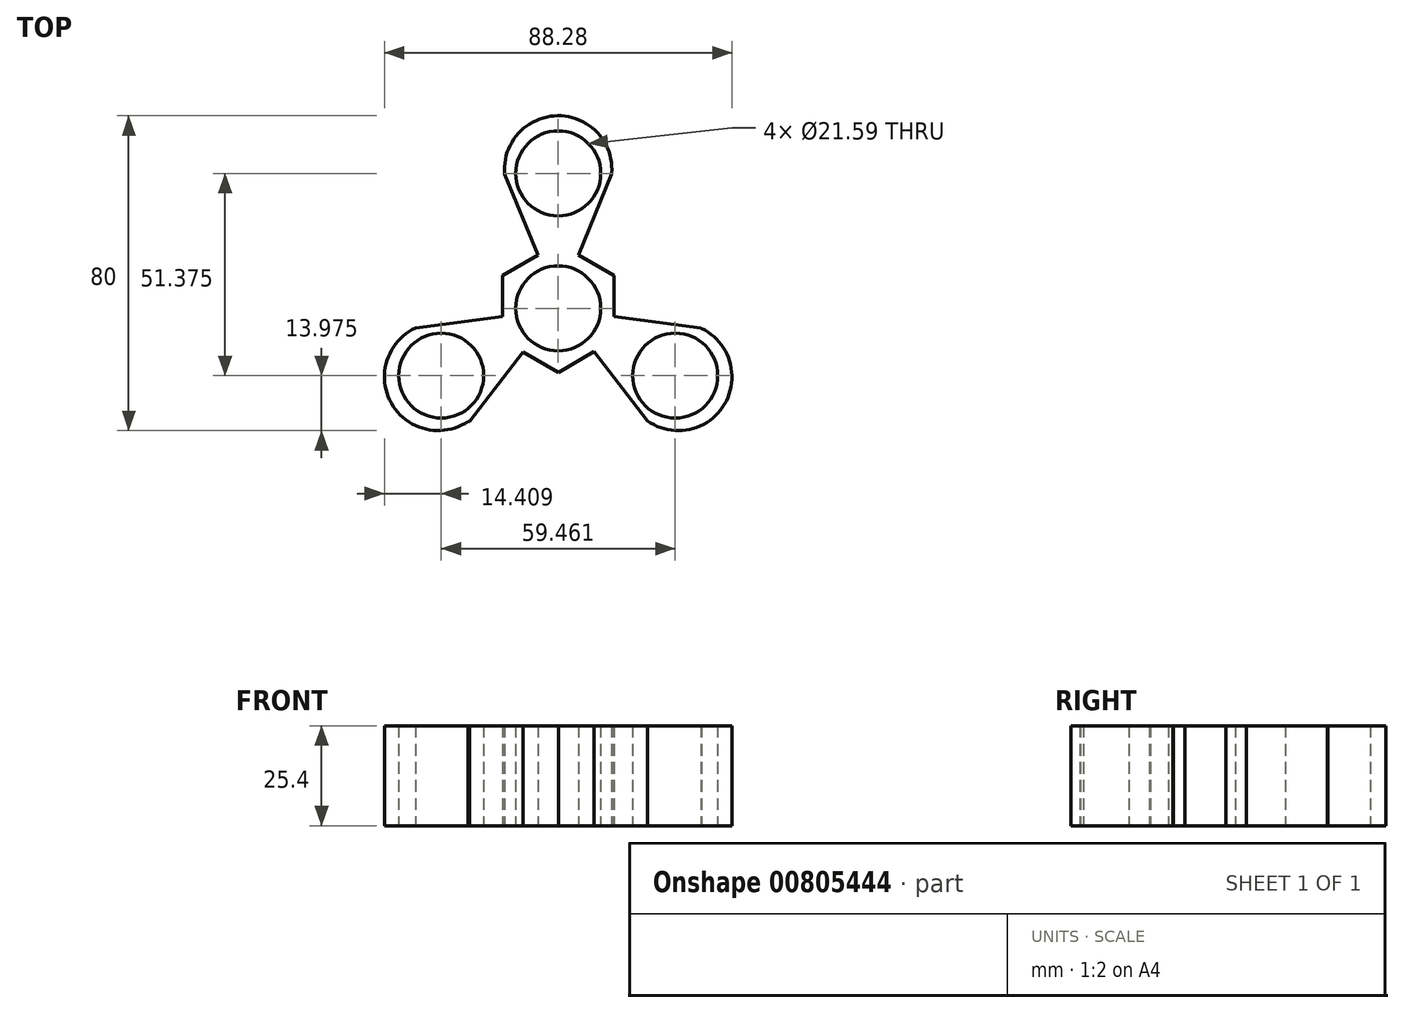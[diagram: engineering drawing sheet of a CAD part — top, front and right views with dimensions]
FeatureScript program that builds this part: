
annotation { "Feature Type Name" : "Feature", "Feature Type Description" : "" }
export const myFeature = defineFeature(function(context is Context, id is Id, definition is map)
    precondition{}
    {
        {
            var Q0;
            Q0=qCreatedBy(makeId("Top.planeOp"),FACE);
            var sketch = newSketch(context, id + "F0", { "sketchPlane" : qUnion([Q0])});
            skCircle(sketch, "E0", {"center": v(0, 0) * mm, "radius": 10.8 * mm});
            skLineSegment(sketch, "E1", {"start": v(0, 34.3) * mm, "end": v(-8, 20.47) * mm});
            skLineSegment(sketch, "E2", {"start": v(-29.73, -17.08) * mm, "end": v(-13.6, -17.08) * mm});
            skLineSegment(sketch, "E3", {"start": v(29.73, -17.08) * mm, "end": v(21.63, -3.09) * mm});
            skCircle(sketch, "E4", {"center": v(0, 34.3) * mm, "radius": 10.8 * mm});
            skCircle(sketch, "E5", {"center": v(-29.73, -17.08) * mm, "radius": 10.8 * mm});
            skCircle(sketch, "E6", {"center": v(29.73, -17.08) * mm, "radius": 10.8 * mm});
            skArc(sketch, "E7", {"start": v(13.6, 34.3) * mm, "mid": v(-0.12, 48.94) * mm, "end": v(-13.6, 34.07) * mm});
            skLineSegment(sketch, "E8", {"start": v(0, 61.27) * mm, "end": v(0, -54.26) * mm});
            skPoint(sketch, "E8.endSnap0", {"position": v(0, -17.08) * mm});
            skLineSegment(sketch, "E9", {"start": v(29.73, -17.08) * mm, "end": v(-43.23, 25.13) * mm});
            skLineSegment(sketch, "E10", {"start": v(-29.73, -17.08) * mm, "end": v(41.97, 24.4) * mm});
            skArc(sketch, "E11.MirrorCS", {"start": v(36.4, -5.11) * mm, "mid": v(42.27, -24.3) * mm, "end": v(22.66, -28.59) * mm});
            skArc(sketch, "E12.MirrorCS", {"start": v(-22.85, -28.7) * mm, "mid": v(-42.39, -24.1) * mm, "end": v(-36.21, -5) * mm});
            skLineSegment(sketch, "E13", {"start": v(-36.21, -5) * mm, "end": v(-14.16, -2.1) * mm});
            skLineSegment(sketch, "E14.MirrorCS", {"start": v(-13.6, 34.07) * mm, "end": v(-5.13, 13.5) * mm});
            skLineSegment(sketch, "E15.MirrorCS", {"start": v(13.6, 34.07) * mm, "end": v(5.13, 13.5) * mm});
            skLineSegment(sketch, "E16.MirrorCS", {"start": v(-0.1, 34.47) * mm, "end": v(8, 20.47) * mm});
            skLineSegment(sketch, "E17.MirrorCS", {"start": v(36.21, -5) * mm, "end": v(14.16, -2.1) * mm});
            skLineSegment(sketch, "E18.MirrorCS", {"start": v(22.66, -28.59) * mm, "end": v(9.05, -11) * mm});
            skLineSegment(sketch, "E19.MirrorCS", {"start": v(-22.48, -28.72) * mm, "end": v(-8.98, -11.05) * mm});
            skLineSegment(sketch, "E20", {"start": v(-14.16, -2.1) * mm, "end": v(-14.16, 8.31) * mm});
            skLineSegment(sketch, "E21", {"start": v(-14.16, 8.31) * mm, "end": v(-5.13, 13.5) * mm});
            skLineSegment(sketch, "E22.MirrorCS", {"start": v(14.16, 8.31) * mm, "end": v(5.13, 13.5) * mm});
            skLineSegment(sketch, "E23.MirrorCS", {"start": v(14.16, -2.1) * mm, "end": v(14.16, 8.31) * mm});
            skLineSegment(sketch, "E24.MirrorCS", {"start": v(-8.98, -11.05) * mm, "end": v(0.05, -16.24) * mm});
            skLineSegment(sketch, "E25.MirrorCS", {"start": v(0.05, -16.24) * mm, "end": v(9.05, -11) * mm});
            skLineSegment(sketch, "E26", {"start": v(13.6, 34.3) * mm, "end": v(13.6, 34.07) * mm});
            skLineSegment(sketch, "E27", {"start": v(-22.85, -28.7) * mm, "end": v(-22.48, -28.72) * mm});
            skLineSegment(sketch, "E28", {"start": v(36.21, -5) * mm, "end": v(36.4, -5.11) * mm});
            skLineSegment(sketch, "E29.trimOffspring", {"start": v(-21.63, -3.09) * mm, "end": v(-29.73, -17.08) * mm});
            skLineSegment(sketch, "E30.trimOffspring", {"start": v(21.63, -3.09) * mm, "end": v(29.63, -16.9) * mm});
            skLineSegment(sketch, "E31.trimOffspring", {"start": v(13.76, -17.08) * mm, "end": v(29.73, -17.08) * mm});
            skLineSegment(sketch, "E32.trimOffspring", {"start": v(8, 20.47) * mm, "end": v(0, 34.3) * mm});
            skSolve(sketch);
        }
        {
            var Q0;
            {var subQ0=sQuery(id+"F0.wireOp",EDGE,"E12.MirrorCS");Q0=makeQuery(id+"F0.imprint","IMPRINT",FACE,{"disambiguationData":[TD([[makeQuery(id+"F0.imprint","IMPRINT",EDGE,{"derivedFrom":subQ0}),-1.0]])]});}
            var Q1;
            {var subQ5=sQuery(id+"F0.wireOp",EDGE,"E2");var subQ11=sQuery(id+"F0.wireOp",EDGE,"E19.MirrorCS");var subQ12=makeQuery(id+"F0.imprint","INTERSECT",VERTEX,{"derivedFrom":[subQ5,subQ11]});Q1=makeQuery(id+"F0.imprint","IMPRINT",FACE,{"disambiguationData":[TD([[makeQuery(id+"F0.imprint","IMPRINT",EDGE,{"disambiguationData":[TD([[subQ12,1.0]])],"derivedFrom":subQ5}),1.0]])]});}
            var Q2;
            {var subQ0=sQuery(id+"F0.wireOp",EDGE,"E20");Q2=makeQuery(id+"F0.imprint","IMPRINT",FACE,{"disambiguationData":[TD([[makeQuery(id+"F0.imprint","IMPRINT",EDGE,{"derivedFrom":subQ0}),-1.0]])]});}
            var Q3;
            {var subQ0=sQuery(id+"F0.wireOp",EDGE,"E21");Q3=makeQuery(id+"F0.imprint","IMPRINT",FACE,{"disambiguationData":[TD([[makeQuery(id+"F0.imprint","IMPRINT",EDGE,{"derivedFrom":subQ0}),-1.0]])]});}
            var Q4;
            {var subQ0=sQuery(id+"F0.wireOp",EDGE,"E22.MirrorCS");Q4=makeQuery(id+"F0.imprint","IMPRINT",FACE,{"disambiguationData":[TD([[makeQuery(id+"F0.imprint","IMPRINT",EDGE,{"derivedFrom":subQ0}),1.0]])]});}
            var Q5;
            {var subQ5=sQuery(id+"F0.wireOp",EDGE,"E26");Q5=makeQuery(id+"F0.imprint","IMPRINT",FACE,{"disambiguationData":[TD([[makeQuery(id+"F0.imprint","IMPRINT",EDGE,{"derivedFrom":subQ5}),-1.0]])]});}
            var Q6;
            {var subQ5=sQuery(id+"F0.wireOp",EDGE,"E1");var subQ7=sQuery(id+"F0.wireOp",EDGE,"E14.MirrorCS");var subQ9=makeQuery(id+"F0.imprint","INTERSECT",VERTEX,{"derivedFrom":[subQ5,subQ7]});Q6=makeQuery(id+"F0.imprint","IMPRINT",FACE,{"disambiguationData":[TD([[makeQuery(id+"F0.imprint","IMPRINT",EDGE,{"disambiguationData":[TD([[subQ9,1.0]])],"derivedFrom":subQ5}),-1.0]])]});}
            var Q7;
            {var subQ0=sQuery(id+"F0.wireOp",EDGE,"E23.MirrorCS");Q7=makeQuery(id+"F0.imprint","IMPRINT",FACE,{"disambiguationData":[TD([[makeQuery(id+"F0.imprint","IMPRINT",EDGE,{"derivedFrom":subQ0}),1.0]])]});}
            var Q8;
            {var subQ0=sQuery(id+"F0.wireOp",EDGE,"E25.MirrorCS");Q8=makeQuery(id+"F0.imprint","IMPRINT",FACE,{"disambiguationData":[TD([[makeQuery(id+"F0.imprint","IMPRINT",EDGE,{"derivedFrom":subQ0}),1.0]])]});}
            var Q9;
            {var subQ5=sQuery(id+"F0.wireOp",EDGE,"E11.MirrorCS");Q9=makeQuery(id+"F0.imprint","IMPRINT",FACE,{"disambiguationData":[TD([[makeQuery(id+"F0.imprint","IMPRINT",EDGE,{"derivedFrom":subQ5}),-1.0]])]});}
            extrude(context, id + "F1", {"entities" : qUnion([Q0, Q1, Q2, Q3, Q4, Q5, Q6, Q7, Q8, Q9]), "depth" : 6.92 * mm, "offsetDistance" : 25.4 * mm});
        }
        {
            var Q0;
            Q0=makeQuery(id+"F1.opExtrude","CAP_FACE",FACE,{"disambiguationData":[OSD([sQuery(id+"F0.wireOp",EDGE,"E4"),sQuery(id+"F0.wireOp",EDGE,"E5"),sQuery(id+"F0.wireOp",EDGE,"E6"),sQuery(id+"F0.wireOp",EDGE,"E7"),sQuery(id+"F0.wireOp",EDGE,"E11.MirrorCS"),sQuery(id+"F0.wireOp",EDGE,"E12.MirrorCS"),sQuery(id+"F0.wireOp",EDGE,"E13"),sQuery(id+"F0.wireOp",EDGE,"E14.MirrorCS"),sQuery(id+"F0.wireOp",EDGE,"E15.MirrorCS"),sQuery(id+"F0.wireOp",EDGE,"E17.MirrorCS"),sQuery(id+"F0.wireOp",EDGE,"E18.MirrorCS"),sQuery(id+"F0.wireOp",EDGE,"E19.MirrorCS"),sQuery(id+"F0.wireOp",EDGE,"E20"),sQuery(id+"F0.wireOp",EDGE,"E21"),sQuery(id+"F0.wireOp",EDGE,"E0"),sQuery(id+"F0.wireOp",EDGE,"E22.MirrorCS"),sQuery(id+"F0.wireOp",EDGE,"E23.MirrorCS"),sQuery(id+"F0.wireOp",EDGE,"E24.MirrorCS"),sQuery(id+"F0.wireOp",EDGE,"E25.MirrorCS"),sQuery(id+"F0.wireOp",EDGE,"E26"),sQuery(id+"F0.wireOp",EDGE,"E27"),sQuery(id+"F0.wireOp",EDGE,"E28")])],"isStart":false});
            var Q1;
            Q1=makeQuery(id+"F1.opExtrude","CAP_FACE",FACE,{"disambiguationData":[OSD([sQuery(id+"F0.wireOp",EDGE,"E4"),sQuery(id+"F0.wireOp",EDGE,"E5"),sQuery(id+"F0.wireOp",EDGE,"E6"),sQuery(id+"F0.wireOp",EDGE,"E7"),sQuery(id+"F0.wireOp",EDGE,"E11.MirrorCS"),sQuery(id+"F0.wireOp",EDGE,"E12.MirrorCS"),sQuery(id+"F0.wireOp",EDGE,"E13"),sQuery(id+"F0.wireOp",EDGE,"E14.MirrorCS"),sQuery(id+"F0.wireOp",EDGE,"E15.MirrorCS"),sQuery(id+"F0.wireOp",EDGE,"E17.MirrorCS"),sQuery(id+"F0.wireOp",EDGE,"E18.MirrorCS"),sQuery(id+"F0.wireOp",EDGE,"E19.MirrorCS"),sQuery(id+"F0.wireOp",EDGE,"E20"),sQuery(id+"F0.wireOp",EDGE,"E21"),sQuery(id+"F0.wireOp",EDGE,"E0"),sQuery(id+"F0.wireOp",EDGE,"E22.MirrorCS"),sQuery(id+"F0.wireOp",EDGE,"E23.MirrorCS"),sQuery(id+"F0.wireOp",EDGE,"E24.MirrorCS"),sQuery(id+"F0.wireOp",EDGE,"E25.MirrorCS"),sQuery(id+"F0.wireOp",EDGE,"E26"),sQuery(id+"F0.wireOp",EDGE,"E27"),sQuery(id+"F0.wireOp",EDGE,"E28")])],"isStart":true});
            fillet(context, id + "F2", {"entities" : qUnion([Q0, Q1]), "radius" : 1.27 * mm, "tangentPropagation" : true, "allowEdgeOverflow" : false});
        }
        {
            var Q0;
            Q0 = qSketchRegion(id + "F0", true);
            var Q1;
            Q1=makeQuery(id+"F2.opFillet","SPLIT",FACE,{"disambiguationData":[OD(0.0)],"derivedFrom":makeQuery(id+"F1.opExtrude","CAP_FACE",FACE,{"disambiguationData":[OSD([sQuery(id+"F0.wireOp",EDGE,"E4"),sQuery(id+"F0.wireOp",EDGE,"E5"),sQuery(id+"F0.wireOp",EDGE,"E6"),sQuery(id+"F0.wireOp",EDGE,"E7"),sQuery(id+"F0.wireOp",EDGE,"E11.MirrorCS"),sQuery(id+"F0.wireOp",EDGE,"E12.MirrorCS"),sQuery(id+"F0.wireOp",EDGE,"E13"),sQuery(id+"F0.wireOp",EDGE,"E14.MirrorCS"),sQuery(id+"F0.wireOp",EDGE,"E15.MirrorCS"),sQuery(id+"F0.wireOp",EDGE,"E17.MirrorCS"),sQuery(id+"F0.wireOp",EDGE,"E18.MirrorCS"),sQuery(id+"F0.wireOp",EDGE,"E19.MirrorCS"),sQuery(id+"F0.wireOp",EDGE,"E20"),sQuery(id+"F0.wireOp",EDGE,"E21"),sQuery(id+"F0.wireOp",EDGE,"E0"),sQuery(id+"F0.wireOp",EDGE,"E22.MirrorCS"),sQuery(id+"F0.wireOp",EDGE,"E23.MirrorCS"),sQuery(id+"F0.wireOp",EDGE,"E24.MirrorCS"),sQuery(id+"F0.wireOp",EDGE,"E25.MirrorCS"),sQuery(id+"F0.wireOp",EDGE,"E26"),sQuery(id+"F0.wireOp",EDGE,"E27"),sQuery(id+"F0.wireOp",EDGE,"E28")])],"isStart":false})});
            var Q2;
            Q2=makeQuery(id+"F2.opFillet","SPLIT",FACE,{"disambiguationData":[OD(2.0)],"derivedFrom":makeQuery(id+"F1.opExtrude","CAP_FACE",FACE,{"disambiguationData":[OSD([sQuery(id+"F0.wireOp",EDGE,"E4"),sQuery(id+"F0.wireOp",EDGE,"E5"),sQuery(id+"F0.wireOp",EDGE,"E6"),sQuery(id+"F0.wireOp",EDGE,"E7"),sQuery(id+"F0.wireOp",EDGE,"E11.MirrorCS"),sQuery(id+"F0.wireOp",EDGE,"E12.MirrorCS"),sQuery(id+"F0.wireOp",EDGE,"E13"),sQuery(id+"F0.wireOp",EDGE,"E14.MirrorCS"),sQuery(id+"F0.wireOp",EDGE,"E15.MirrorCS"),sQuery(id+"F0.wireOp",EDGE,"E17.MirrorCS"),sQuery(id+"F0.wireOp",EDGE,"E18.MirrorCS"),sQuery(id+"F0.wireOp",EDGE,"E19.MirrorCS"),sQuery(id+"F0.wireOp",EDGE,"E20"),sQuery(id+"F0.wireOp",EDGE,"E21"),sQuery(id+"F0.wireOp",EDGE,"E0"),sQuery(id+"F0.wireOp",EDGE,"E22.MirrorCS"),sQuery(id+"F0.wireOp",EDGE,"E23.MirrorCS"),sQuery(id+"F0.wireOp",EDGE,"E24.MirrorCS"),sQuery(id+"F0.wireOp",EDGE,"E25.MirrorCS"),sQuery(id+"F0.wireOp",EDGE,"E26"),sQuery(id+"F0.wireOp",EDGE,"E27"),sQuery(id+"F0.wireOp",EDGE,"E28")])],"isStart":false})});
            extrude(context, id + "F3", {"entities" : qUnion([Q0, Q1, Q2]), "operationType" : NewBodyOperationType.REMOVE, "oppositeDirection" : true, "depth" : 25.4 * mm, "offsetDistance" : 25.4 * mm});
        }
        {
            var Q0;
            Q0 = qSketchRegion(id + "F0", true);
            var Q1;
            Q1=makeQuery(id+"F2.opFillet","SPLIT",FACE,{"disambiguationData":[OD(1.0)],"derivedFrom":makeQuery(id+"F1.opExtrude","CAP_FACE",FACE,{"disambiguationData":[OSD([sQuery(id+"F0.wireOp",EDGE,"E4"),sQuery(id+"F0.wireOp",EDGE,"E5"),sQuery(id+"F0.wireOp",EDGE,"E6"),sQuery(id+"F0.wireOp",EDGE,"E7"),sQuery(id+"F0.wireOp",EDGE,"E11.MirrorCS"),sQuery(id+"F0.wireOp",EDGE,"E12.MirrorCS"),sQuery(id+"F0.wireOp",EDGE,"E13"),sQuery(id+"F0.wireOp",EDGE,"E14.MirrorCS"),sQuery(id+"F0.wireOp",EDGE,"E15.MirrorCS"),sQuery(id+"F0.wireOp",EDGE,"E17.MirrorCS"),sQuery(id+"F0.wireOp",EDGE,"E18.MirrorCS"),sQuery(id+"F0.wireOp",EDGE,"E19.MirrorCS"),sQuery(id+"F0.wireOp",EDGE,"E20"),sQuery(id+"F0.wireOp",EDGE,"E21"),sQuery(id+"F0.wireOp",EDGE,"E0"),sQuery(id+"F0.wireOp",EDGE,"E22.MirrorCS"),sQuery(id+"F0.wireOp",EDGE,"E23.MirrorCS"),sQuery(id+"F0.wireOp",EDGE,"E24.MirrorCS"),sQuery(id+"F0.wireOp",EDGE,"E25.MirrorCS"),sQuery(id+"F0.wireOp",EDGE,"E26"),sQuery(id+"F0.wireOp",EDGE,"E27"),sQuery(id+"F0.wireOp",EDGE,"E28")])],"isStart":false})});
            extrude(context, id + "F4", {"entities" : qUnion([Q0, Q1]), "operationType" : NewBodyOperationType.ADD, "depth" : 25.4 * mm, "offsetDistance" : 25.4 * mm});
        }
    });
